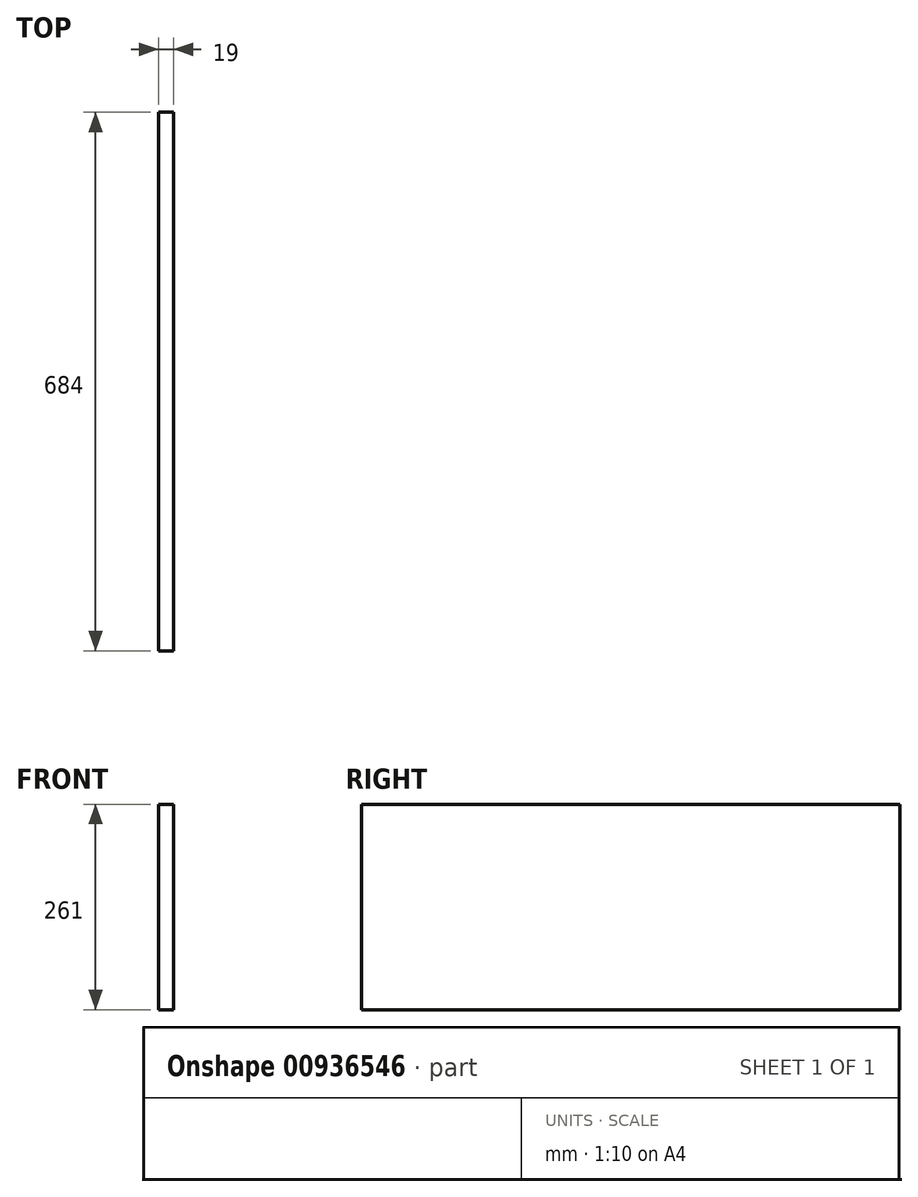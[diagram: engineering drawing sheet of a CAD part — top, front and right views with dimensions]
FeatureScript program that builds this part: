
annotation { "Feature Type Name" : "Feature", "Feature Type Description" : "" }
export const myFeature = defineFeature(function(context is Context, id is Id, definition is map)
    precondition{}
    {
        {
            var Q0;
            Q0=qCreatedBy(makeId("Front.planeOp"),FACE);
            var sketch = newSketch(context, id + "F0", { "sketchPlane" : qUnion([Q0])});
            skLineSegment(sketch, "E0.bottom", {"start": v(9.5, 130.5) * mm, "end": v(-9.5, 130.5) * mm});
            skLineSegment(sketch, "E0.top", {"start": v(9.5, -130.5) * mm, "end": v(-9.5, -130.5) * mm});
            skLineSegment(sketch, "E0.left", {"start": v(9.5, 130.5) * mm, "end": v(9.5, -130.5) * mm});
            skLineSegment(sketch, "E0.right", {"start": v(-9.5, 130.5) * mm, "end": v(-9.5, -130.5) * mm});
            skPoint(sketch, "E0.middle", {"position": v(0, 0) * mm});
            skSolve(sketch);
        }
        {
            var Q0;
            Q0=qSketchRegion(id+"F0",true);
            extrude(context, id + "F1", {"entities" : qUnion([Q0]), "depth" : 684 * mm, "offsetDistance" : 25 * mm});
        }
    });
